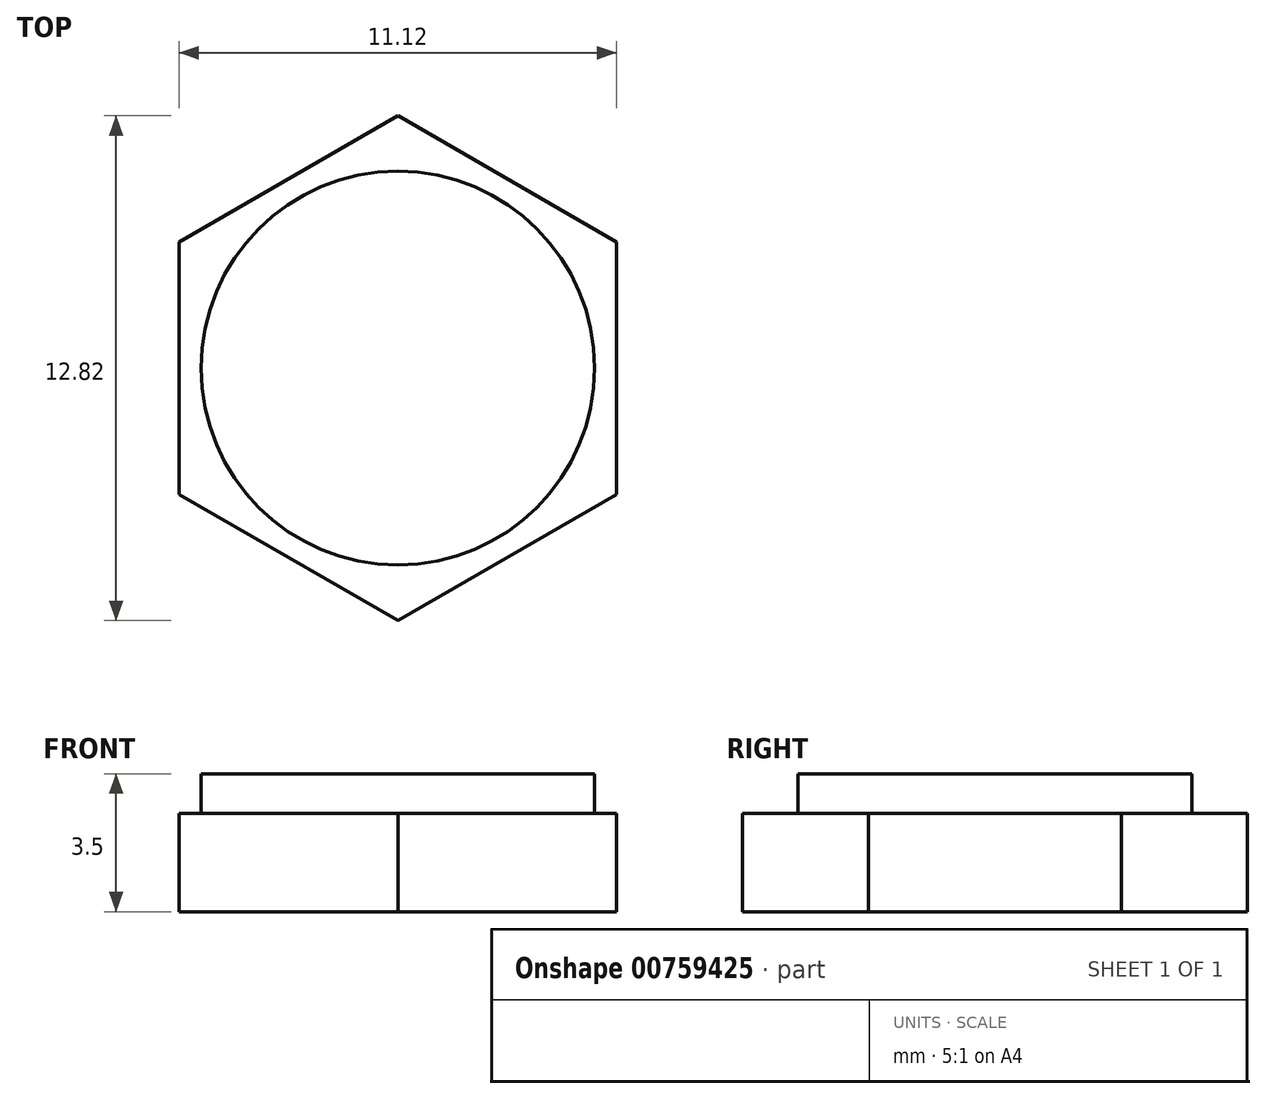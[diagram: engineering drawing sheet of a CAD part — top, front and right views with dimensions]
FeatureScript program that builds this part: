
annotation { "Feature Type Name" : "Feature", "Feature Type Description" : "" }
export const myFeature = defineFeature(function(context is Context, id is Id, definition is map)
    precondition{}
    {
        {
            var Q0;
            Q0=qCreatedBy(makeId("Top.planeOp"),FACE);
            var sketch = newSketch(context, id + "F0", { "sketchPlane" : qUnion([Q0])});
            skCircle(sketch, "E0.cCircle", {"center": v(0, 0) * mm, "radius": 5.55 * mm, "construction": true});
            skLineSegment(sketch, "E0.0", {"start": v(5.55, 3.2) * mm, "end": v(5.55, -3.2) * mm});
            skLineSegment(sketch, "E0.1", {"start": v(5.56, -3.2) * mm, "end": v(0, -6.41) * mm});
            skLineSegment(sketch, "E0.2", {"start": v(0, -6.41) * mm, "end": v(-5.55, -3.2) * mm});
            skLineSegment(sketch, "E0.3", {"start": v(-5.55, -3.2) * mm, "end": v(-5.56, 3.2) * mm});
            skLineSegment(sketch, "E0.4", {"start": v(-5.56, 3.2) * mm, "end": v(0, 6.41) * mm});
            skLineSegment(sketch, "E0.5", {"start": v(0, 6.41) * mm, "end": v(5.55, 3.2) * mm});
            skPoint(sketch, "E0.0.midPoint", {"position": v(5.55, 0) * mm});
            skCircle(sketch, "E1", {"center": v(0, 0) * mm, "radius": 5 * mm});
            skSolve(sketch);
        }
        {
            var Q0;
            Q0=makeQuery(id+"F0.imprint","IMPRINT",FACE,{"disambiguationData":[TD([[makeQuery(id+"F0.imprint","IMPRINT",EDGE,{"derivedFrom":sQuery(id+"F0.wireOp",EDGE,"E1")}),1.0]])]});
            extrude(context, id + "F1", {"entities" : qUnion([Q0]), "depth" : 3.5 * mm, "offsetDistance" : 25 * mm});
        }
        {
            var Q0;
            Q0 = qSketchRegion(id + "F0", true);
            extrude(context, id + "F2", {"entities" : qUnion([Q0]), "operationType" : NewBodyOperationType.ADD, "depth" : 2.5 * mm, "offsetDistance" : 25 * mm});
        }
    });
